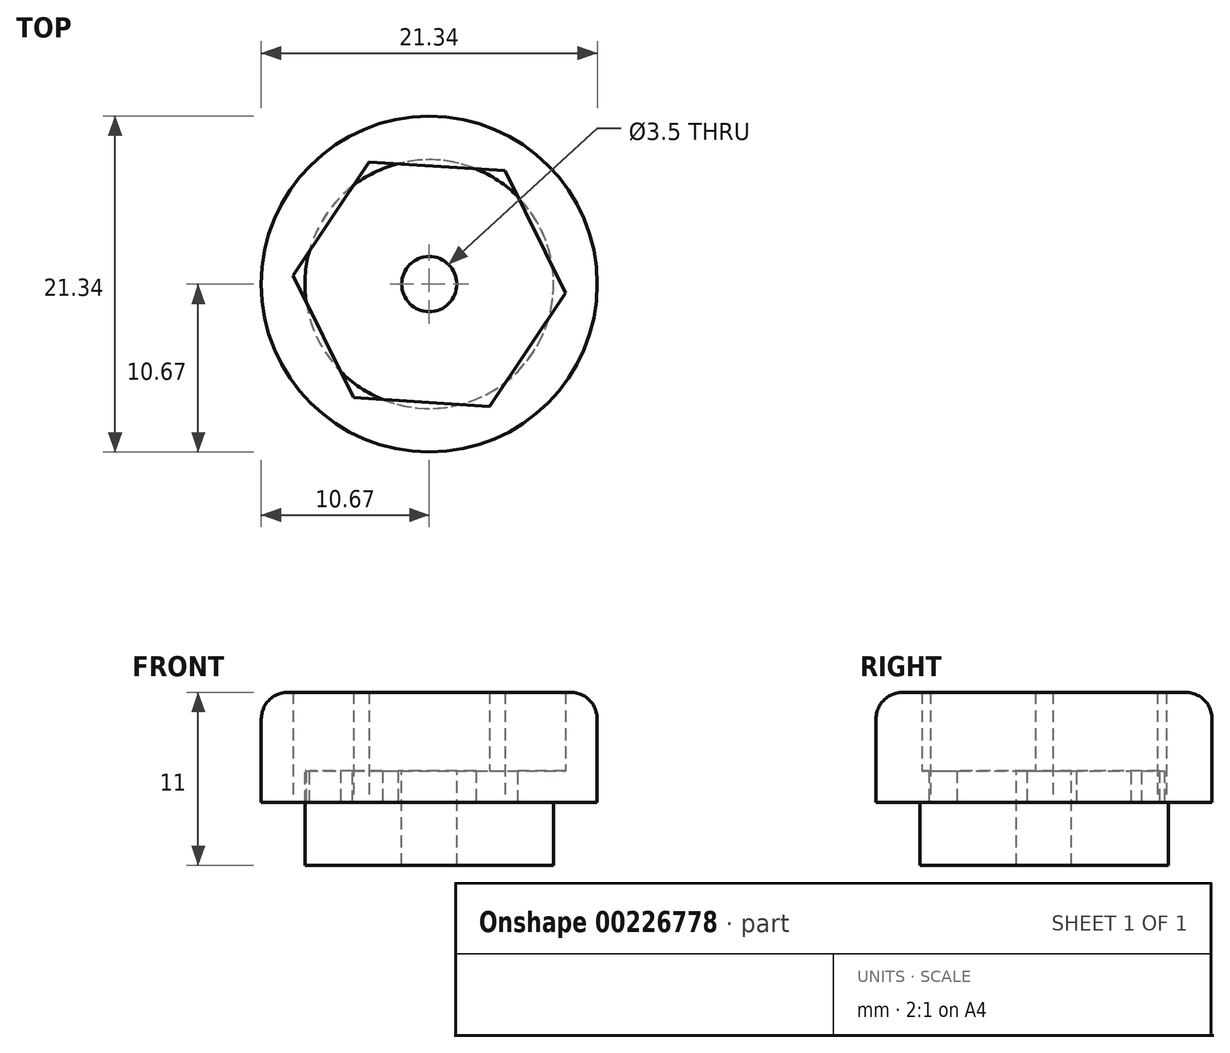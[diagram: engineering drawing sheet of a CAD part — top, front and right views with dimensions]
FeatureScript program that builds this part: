
annotation { "Feature Type Name" : "Feature", "Feature Type Description" : "" }
export const myFeature = defineFeature(function(context is Context, id is Id, definition is map)
    precondition{}
    {
        {
            var Q0;
            Q0=qCreatedBy(makeId("Top.planeOp"),FACE);
            var sketch = newSketch(context, id + "F0", { "sketchPlane" : qUnion([Q0])});
            skCircle(sketch, "E0", {"center": v(0, 0) * mm, "radius": 10.67 * mm});
            skCircle(sketch, "E1.cCircle", {"center": v(0, 0) * mm, "radius": 8.66 * mm, "construction": true});
            skLineSegment(sketch, "E1.0", {"start": v(-8.64, 0.56) * mm, "end": v(-3.84, 7.76) * mm});
            skLineSegment(sketch, "E1.1", {"start": v(-3.84, 7.76) * mm, "end": v(4.8, 7.2) * mm});
            skLineSegment(sketch, "E1.2", {"start": v(4.8, 7.2) * mm, "end": v(8.64, -0.56) * mm});
            skLineSegment(sketch, "E1.3", {"start": v(8.64, -0.56) * mm, "end": v(3.84, -7.76) * mm});
            skLineSegment(sketch, "E1.4", {"start": v(3.84, -7.76) * mm, "end": v(-4.8, -7.2) * mm});
            skLineSegment(sketch, "E1.5", {"start": v(-4.8, -7.2) * mm, "end": v(-8.64, 0.56) * mm});
            skSolve(sketch);
        }
        {
            var Q0;
            Q0=makeQuery(id+"F0.imprint","IMPRINT",FACE,{"disambiguationData":[TD([[makeQuery(id+"F0.imprint","IMPRINT",EDGE,{"derivedFrom":sQuery(id+"F0.wireOp",EDGE,"E0")}),1.0]])]});
            extrude(context, id + "F1", {"entities" : qUnion([Q0]), "depth" : 7 * mm, "offsetDistance" : 25 * mm});
        }
        {
            var Q0;
            Q0=makeQuery(id+"F1.opExtrude","CAP_FACE",FACE,{"disambiguationData":[OSD([sQuery(id+"F0.wireOp",EDGE,"E0"),sQuery(id+"F0.wireOp",EDGE,"E1.0"),sQuery(id+"F0.wireOp",EDGE,"E1.1"),sQuery(id+"F0.wireOp",EDGE,"E1.2"),sQuery(id+"F0.wireOp",EDGE,"E1.3"),sQuery(id+"F0.wireOp",EDGE,"E1.4"),sQuery(id+"F0.wireOp",EDGE,"E1.5")])],"isStart":true});
            cPlane(context, id + "F2", {"entities" : qUnion([Q0]), "cplaneType" : CPlaneType.OFFSET, "offset" : 2 * mm, "oppositeDirection" : true, "width" : 150 * mm, "height" : 150 * mm});
        }
        {
            var Q0;
            Q0=qCreatedBy(id+"F2.planeOp",FACE);
            var sketch = newSketch(context, id + "F3", { "sketchPlane" : qUnion([Q0])});
            skCircle(sketch, "E2", {"center": v(0, 0) * mm, "radius": 7.9 * mm});
            skCircle(sketch, "E3.cCircle", {"center": v(0, 0) * mm, "radius": 7.5 * mm, "construction": true});
            skLineSegment(sketch, "E3.0", {"start": v(3.84, 7.76) * mm, "end": v(8.64, 0.56) * mm});
            skLineSegment(sketch, "E3.1", {"start": v(8.64, 0.56) * mm, "end": v(4.8, -7.2) * mm});
            skLineSegment(sketch, "E3.2", {"start": v(4.8, -7.2) * mm, "end": v(-3.84, -7.76) * mm});
            skLineSegment(sketch, "E3.3", {"start": v(-3.84, -7.76) * mm, "end": v(-8.64, -0.56) * mm});
            skLineSegment(sketch, "E3.4", {"start": v(-8.64, -0.56) * mm, "end": v(-4.8, 7.2) * mm});
            skLineSegment(sketch, "E3.5", {"start": v(-4.8, 7.2) * mm, "end": v(3.84, 7.76) * mm});
            skPoint(sketch, "E3.0.midPoint", {"position": v(6.24, 4.16) * mm});
            skSolve(sketch);
        }
        {
            var Q0;
            {var subQ0=sQuery(id+"F3.wireOp",EDGE,"E3.0");var subQ1=sQuery(id+"F3.wireOp",EDGE,"E2");var subQ2=makeQuery(id+"F3.imprint","INTERSECT",VERTEX,{"disambiguationData":[OD(0.0)],"derivedFrom":[subQ1,subQ0]});Q0=makeQuery(id+"F3.imprint","IMPRINT",FACE,{"disambiguationData":[TD([[makeQuery(id+"F3.imprint","IMPRINT",EDGE,{"disambiguationData":[TD([[subQ2,-1.0]])],"derivedFrom":subQ1}),-1.0]])]});}
            var Q1;
            {var subQ0=sQuery(id+"F3.wireOp",EDGE,"E3.5");var subQ1=sQuery(id+"F3.wireOp",EDGE,"E2");var subQ2=makeQuery(id+"F3.imprint","INTERSECT",VERTEX,{"disambiguationData":[OD(1.0)],"derivedFrom":[subQ1,subQ0]});Q1=makeQuery(id+"F3.imprint","IMPRINT",FACE,{"disambiguationData":[TD([[makeQuery(id+"F3.imprint","IMPRINT",EDGE,{"disambiguationData":[TD([[subQ2,-1.0]])],"derivedFrom":subQ1}),-1.0]])]});}
            var Q2;
            {var subQ0=sQuery(id+"F3.wireOp",EDGE,"E3.4");var subQ1=sQuery(id+"F3.wireOp",EDGE,"E2");var subQ2=makeQuery(id+"F3.imprint","INTERSECT",VERTEX,{"disambiguationData":[OD(1.0)],"derivedFrom":[subQ1,subQ0]});Q2=makeQuery(id+"F3.imprint","IMPRINT",FACE,{"disambiguationData":[TD([[makeQuery(id+"F3.imprint","IMPRINT",EDGE,{"disambiguationData":[TD([[subQ2,-1.0]])],"derivedFrom":subQ1}),-1.0]])]});}
            var Q3;
            {var subQ0=sQuery(id+"F3.wireOp",EDGE,"E3.3");var subQ1=sQuery(id+"F3.wireOp",EDGE,"E2");var subQ2=makeQuery(id+"F3.imprint","INTERSECT",VERTEX,{"disambiguationData":[OD(1.0)],"derivedFrom":[subQ1,subQ0]});Q3=makeQuery(id+"F3.imprint","IMPRINT",FACE,{"disambiguationData":[TD([[makeQuery(id+"F3.imprint","IMPRINT",EDGE,{"disambiguationData":[TD([[subQ2,-1.0]])],"derivedFrom":subQ1}),-1.0]])]});}
            var Q4;
            {var subQ0=sQuery(id+"F3.wireOp",EDGE,"E3.0");var subQ1=sQuery(id+"F3.wireOp",EDGE,"E2");var subQ2=makeQuery(id+"F3.imprint","INTERSECT",VERTEX,{"disambiguationData":[OD(1.0)],"derivedFrom":[subQ1,subQ0]});Q4=makeQuery(id+"F3.imprint","IMPRINT",FACE,{"disambiguationData":[TD([[makeQuery(id+"F3.imprint","IMPRINT",EDGE,{"disambiguationData":[TD([[subQ2,1.0]])],"derivedFrom":subQ1}),-1.0]])]});}
            var Q5;
            {var subQ0=sQuery(id+"F3.wireOp",EDGE,"E3.2");var subQ1=sQuery(id+"F3.wireOp",EDGE,"E2");var subQ2=makeQuery(id+"F3.imprint","INTERSECT",VERTEX,{"disambiguationData":[OD(1.0)],"derivedFrom":[subQ1,subQ0]});Q5=makeQuery(id+"F3.imprint","IMPRINT",FACE,{"disambiguationData":[TD([[makeQuery(id+"F3.imprint","IMPRINT",EDGE,{"disambiguationData":[TD([[subQ2,-1.0]])],"derivedFrom":subQ1}),-1.0]])]});}
            extrude(context, id + "F4", {"entities" : qUnion([Q0, Q1, Q2, Q3, Q4, Q5]), "operationType" : NewBodyOperationType.ADD, "depth" : 2 * mm, "offsetDistance" : 25 * mm});
        }
        {
            var Q0;
            Q0=makeQuery(id+"F4.opExtrude","CAP_FACE",FACE,{"disambiguationData":[OSD([sQuery(id+"F3.wireOp",EDGE,"E3.0"),sQuery(id+"F3.wireOp",EDGE,"E3.1"),sQuery(id+"F3.wireOp",EDGE,"E3.2"),sQuery(id+"F3.wireOp",EDGE,"E3.3"),sQuery(id+"F3.wireOp",EDGE,"E3.4"),sQuery(id+"F3.wireOp",EDGE,"E3.5")])],"isStart":true});
            var sketch = newSketch(context, id + "F5", { "sketchPlane" : qUnion([Q0])});
            skCircle(sketch, "E4", {"center": v(0, 0) * mm, "radius": 1.75 * mm});
            skSolve(sketch);
        }
        {
            var Q0;
            {var subQ0=sQuery(id+"F3.wireOp",EDGE,"E3.1");var subQ1=sQuery(id+"F3.wireOp",EDGE,"E3.0");var subQ2=sQuery(id+"F3.wireOp",EDGE,"E2");var subQ3=sQuery(id+"F3.wireOp",EDGE,"E3.2");var subQ4=sQuery(id+"F3.wireOp",EDGE,"E3.3");var subQ5=sQuery(id+"F3.wireOp",EDGE,"E3.4");var subQ6=sQuery(id+"F3.wireOp",EDGE,"E3.5");Q0=makeQuery(id+"F4.boolean.opBoolean","MERGE",FACE,{"derivedFrom":[makeQuery(id+"F1.opExtrude","CAP_FACE",FACE,{"disambiguationData":[OSD([sQuery(id+"F0.wireOp",EDGE,"E0"),sQuery(id+"F0.wireOp",EDGE,"E1.0"),sQuery(id+"F0.wireOp",EDGE,"E1.1"),sQuery(id+"F0.wireOp",EDGE,"E1.2"),sQuery(id+"F0.wireOp",EDGE,"E1.3"),sQuery(id+"F0.wireOp",EDGE,"E1.4"),sQuery(id+"F0.wireOp",EDGE,"E1.5")])],"isStart":true}),makeQuery(id+"F4.opExtrude","CAP_FACE",FACE,{"disambiguationData":[OSD([subQ2,subQ1,subQ6])],"isStart":false}),makeQuery(id+"F4.opExtrude","CAP_FACE",FACE,{"disambiguationData":[OSD([subQ2,subQ5,subQ6])],"isStart":false}),makeQuery(id+"F4.opExtrude","CAP_FACE",FACE,{"disambiguationData":[OSD([subQ2,subQ4,subQ5])],"isStart":false}),makeQuery(id+"F4.opExtrude","CAP_FACE",FACE,{"disambiguationData":[OSD([subQ2,subQ3,subQ4])],"isStart":false}),makeQuery(id+"F4.opExtrude","CAP_FACE",FACE,{"disambiguationData":[OSD([subQ2,subQ0,subQ3])],"isStart":false}),makeQuery(id+"F4.opExtrude","CAP_FACE",FACE,{"disambiguationData":[OSD([subQ2,subQ1,subQ0])],"isStart":false})]});}
            var sketch = newSketch(context, id + "F6", { "sketchPlane" : qUnion([Q0])});
            skCircle(sketch, "E5", {"center": v(0, 0) * mm, "radius": 7.9 * mm});
            skCircle(sketch, "E6.cCircle", {"center": v(0, 0) * mm, "radius": 7.5 * mm, "construction": true});
            skLineSegment(sketch, "E6.0", {"start": v(4.8, -7.2) * mm, "end": v(-3.84, -7.76) * mm});
            skLineSegment(sketch, "E6.1", {"start": v(-3.84, -7.76) * mm, "end": v(-8.64, -0.56) * mm});
            skLineSegment(sketch, "E6.2", {"start": v(-8.64, -0.56) * mm, "end": v(-4.8, 7.2) * mm});
            skLineSegment(sketch, "E6.3", {"start": v(-4.8, 7.2) * mm, "end": v(3.84, 7.76) * mm});
            skLineSegment(sketch, "E6.4", {"start": v(3.84, 7.76) * mm, "end": v(8.64, 0.56) * mm});
            skLineSegment(sketch, "E6.5", {"start": v(8.64, 0.56) * mm, "end": v(4.8, -7.2) * mm});
            skPoint(sketch, "E6.0.midPoint", {"position": v(0.48, -7.48) * mm});
            skSolve(sketch);
        }
        {
            var Q0;
            {var subQ0=sQuery(id+"F6.wireOp",EDGE,"E6.4");var subQ1=sQuery(id+"F6.wireOp",EDGE,"E5");var subQ2=makeQuery(id+"F6.imprint","INTERSECT",VERTEX,{"disambiguationData":[OD(0.0)],"derivedFrom":[subQ1,subQ0]});Q0=makeQuery(id+"F6.imprint","IMPRINT",FACE,{"disambiguationData":[TD([[makeQuery(id+"F6.imprint","IMPRINT",EDGE,{"disambiguationData":[TD([[subQ2,1.0]])],"derivedFrom":subQ1}),1.0]])]});}
            var Q1;
            {var subQ0=sQuery(id+"F6.wireOp",EDGE,"E6.5");var subQ1=sQuery(id+"F6.wireOp",EDGE,"E5");var subQ2=makeQuery(id+"F6.imprint","INTERSECT",VERTEX,{"disambiguationData":[OD(0.0)],"derivedFrom":[subQ1,subQ0]});Q1=makeQuery(id+"F6.imprint","IMPRINT",FACE,{"disambiguationData":[TD([[makeQuery(id+"F6.imprint","IMPRINT",EDGE,{"disambiguationData":[TD([[subQ2,-1.0]])],"derivedFrom":subQ1}),1.0]])]});}
            var Q2;
            {var subQ0=sQuery(id+"F6.wireOp",EDGE,"E6.0");var subQ1=sQuery(id+"F6.wireOp",EDGE,"E5");var subQ2=makeQuery(id+"F6.imprint","INTERSECT",VERTEX,{"disambiguationData":[OD(0.0)],"derivedFrom":[subQ1,subQ0]});Q2=makeQuery(id+"F6.imprint","IMPRINT",FACE,{"disambiguationData":[TD([[makeQuery(id+"F6.imprint","IMPRINT",EDGE,{"disambiguationData":[TD([[subQ2,-1.0]])],"derivedFrom":subQ1}),1.0]])]});}
            var Q3;
            {var subQ0=sQuery(id+"F6.wireOp",EDGE,"E6.1");var subQ1=sQuery(id+"F6.wireOp",EDGE,"E5");var subQ2=makeQuery(id+"F6.imprint","INTERSECT",VERTEX,{"disambiguationData":[OD(0.0)],"derivedFrom":[subQ1,subQ0]});Q3=makeQuery(id+"F6.imprint","IMPRINT",FACE,{"disambiguationData":[TD([[makeQuery(id+"F6.imprint","IMPRINT",EDGE,{"disambiguationData":[TD([[subQ2,-1.0]])],"derivedFrom":subQ1}),1.0]])]});}
            var Q4;
            {var subQ0=sQuery(id+"F6.wireOp",EDGE,"E6.2");var subQ1=sQuery(id+"F6.wireOp",EDGE,"E5");var subQ2=makeQuery(id+"F6.imprint","INTERSECT",VERTEX,{"disambiguationData":[OD(0.0)],"derivedFrom":[subQ1,subQ0]});Q4=makeQuery(id+"F6.imprint","IMPRINT",FACE,{"disambiguationData":[TD([[makeQuery(id+"F6.imprint","IMPRINT",EDGE,{"disambiguationData":[TD([[subQ2,-1.0]])],"derivedFrom":subQ1}),1.0]])]});}
            var Q5;
            {var subQ0=sQuery(id+"F6.wireOp",EDGE,"E6.3");var subQ1=sQuery(id+"F6.wireOp",EDGE,"E5");var subQ2=makeQuery(id+"F6.imprint","INTERSECT",VERTEX,{"disambiguationData":[OD(0.0)],"derivedFrom":[subQ1,subQ0]});Q5=makeQuery(id+"F6.imprint","IMPRINT",FACE,{"disambiguationData":[TD([[makeQuery(id+"F6.imprint","IMPRINT",EDGE,{"disambiguationData":[TD([[subQ2,-1.0]])],"derivedFrom":subQ1}),1.0]])]});}
            extrude(context, id + "F7", {"entities" : qUnion([Q0, Q1, Q2, Q3, Q4, Q5]), "operationType" : NewBodyOperationType.REMOVE, "oppositeDirection" : true, "depth" : 2 * mm, "offsetDistance" : 25 * mm});
        }
        {
            var Q0;
            Q0=qCreatedBy(id+"F2.planeOp",FACE);
            var sketch = newSketch(context, id + "F8", { "sketchPlane" : qUnion([Q0])});
            skCircle(sketch, "E7", {"center": v(0, 0) * mm, "radius": 7.9 * mm});
            skSolve(sketch);
        }
        {
            var Q0;
            Q0=makeQuery(id+"F8.imprint","IMPRINT",FACE,{"disambiguationData":[TD([[makeQuery(id+"F8.imprint","IMPRINT",EDGE,{"derivedFrom":sQuery(id+"F8.wireOp",EDGE,"E7")}),1.0]])]});
            extrude(context, id + "F9", {"entities" : qUnion([Q0]), "operationType" : NewBodyOperationType.ADD, "depth" : 6 * mm, "offsetDistance" : 25 * mm});
        }
        {
            var Q0;
            Q0=makeQuery(id+"F5.imprint","IMPRINT",FACE,{"disambiguationData":[TD([[makeQuery(id+"F5.imprint","IMPRINT",EDGE,{"derivedFrom":sQuery(id+"F5.wireOp",EDGE,"E4")}),1.0]])]});
            extrude(context, id + "F10", {"entities" : qUnion([Q0]), "operationType" : NewBodyOperationType.REMOVE, "oppositeDirection" : true, "depth" : 25 * mm, "offsetDistance" : 25 * mm});
        }
        {
            var Q0;
            Q0=makeQuery(id+"F1.opExtrude","CAP_EDGE",EDGE,{"disambiguationData":[OSD([sQuery(id+"F0.wireOp",EDGE,"E0")])],"isStart":false});
            fillet(context, id + "F11", {"entities" : qUnion([Q0]), "radius" : 1.7 * mm, "tangentPropagation" : true, "allowEdgeOverflow" : false});
        }
    });
